FCSTD DOCUMENT  (FreeCAD 0.19R24276 (Git))
Label: Master_sketch_3
License: All rights reserved
LicenseURL: http://en.wikipedia.org/wiki/All_rights_reserved
objects: Sketcher::SketchObject×1, PartDesign::Body×1
note: 2 computed .brp shape members not serialized (recipe doc carries the construction recipe); baked Part::Feature solids carry a one-line shape summary decoded from their .brp

FEATURE [Sketcher::SketchObject] Sketch
  FullyConstrained = false
  MapMode = 5
  Support = -> [XY_Plane]
  sketch-geometry (160):
    g0: Circle CenterX=0 CenterY=0 CenterZ=0 NormalX=0 NormalY=0 NormalZ=1 AngleXU=0 Radius=30
    g1: Circle CenterX=0 CenterY=0 CenterZ=0 NormalX=0 NormalY=0 NormalZ=1 AngleXU=0 Radius=100
    g2: Circle CenterX=0 CenterY=-150 CenterZ=0 NormalX=0 NormalY=0 NormalZ=1 AngleXU=0 Radius=30
    g3: LineSegment StartX=-29.8748 StartY=-152.738 StartZ=0 EndX=-29.3845 EndY=-6.04557 EndZ=0
    g4: LineSegment StartX=29.8846 StartY=-152.629 StartZ=0 EndX=28.8668 EndY=-8.16756 EndZ=0
    g5: LineSegment StartX=0 StartY=0 StartZ=0 EndX=-44.858 EndY=-3.57179 EndZ=0
    g6: LineSegment StartX=0 StartY=0 StartZ=0 EndX=44.858 EndY=3.57179 EndZ=0
    g7: Circle CenterX=-44.858 CenterY=-3.57179 CenterZ=0 NormalX=0 NormalY=0 NormalZ=1 AngleXU=0 Radius=44
    g8: Circle CenterX=44.858 CenterY=3.57179 CenterZ=0 NormalX=0 NormalY=0 NormalZ=1 AngleXU=0 Radius=44
    g9: LineSegment StartX=0 StartY=0 StartZ=0 EndX=-29.9053 EndY=-2.38119 EndZ=0
    g10: Circle CenterX=-44.858 CenterY=-3.57179 CenterZ=0 NormalX=0 NormalY=0 NormalZ=1 AngleXU=0 Radius=12.5
    g11: Circle CenterX=0 CenterY=0 CenterZ=0 NormalX=0 NormalY=0 NormalZ=1 AngleXU=0 Radius=12.5
    g12: LineSegment StartX=-45.8502 StartY=8.88878 StartZ=0 EndX=-0.992163 EndY=12.4606 EndZ=0
    g13: LineSegment StartX=0.992163 StartY=-12.4606 StartZ=0 EndX=-43.8659 EndY=-16.0323 EndZ=0
    g14: Circle CenterX=44.858 CenterY=3.57179 CenterZ=0 NormalX=0 NormalY=0 NormalZ=1 AngleXU=0 Radius=21.9437
    g15: LineSegment StartX=279.194 StartY=89.253 StartZ=0 EndX=359.194 EndY=89.253 EndZ=0
    g16: LineSegment StartX=359.194 StartY=89.253 StartZ=0 EndX=359.194 EndY=78.253 EndZ=0
    g17: LineSegment StartX=359.194 StartY=78.253 StartZ=0 EndX=279.194 EndY=78.253 EndZ=0
    g18: LineSegment StartX=279.194 StartY=78.253 StartZ=0 EndX=279.194 EndY=89.253 EndZ=0
    g19: LineSegment StartX=294.194 StartY=89.253 StartZ=0 EndX=294.194 EndY=78.253 EndZ=0
    g20: LineSegment StartX=344.194 StartY=89.253 StartZ=0 EndX=344.194 EndY=78.253 EndZ=0
    g21: LineSegment StartX=279.194 StartY=78.253 StartZ=0 EndX=294.194 EndY=89.253 EndZ=0
    g22: LineSegment StartX=279.194 StartY=89.253 StartZ=0 EndX=294.194 EndY=78.253 EndZ=0
    g23: LineSegment StartX=344.194 StartY=78.253 StartZ=0 EndX=359.194 EndY=89.253 EndZ=0
    g24: LineSegment StartX=344.194 StartY=89.253 StartZ=0 EndX=359.194 EndY=78.253 EndZ=0
    g25: LineSegment StartX=279.194 StartY=107.893 StartZ=0 EndX=359.194 EndY=107.893 EndZ=0
    g26: LineSegment StartX=359.194 StartY=107.893 StartZ=0 EndX=359.194 EndY=118.893 EndZ=0
    g27: LineSegment StartX=359.194 StartY=118.893 StartZ=0 EndX=279.194 EndY=118.893 EndZ=0
    g28: LineSegment StartX=279.194 StartY=118.893 StartZ=0 EndX=279.194 EndY=107.893 EndZ=0
    g29: LineSegment StartX=294.194 StartY=107.893 StartZ=0 EndX=294.194 EndY=118.893 EndZ=0
    g30: LineSegment StartX=344.194 StartY=107.893 StartZ=0 EndX=344.194 EndY=118.893 EndZ=0
    g31: LineSegment StartX=279.194 StartY=118.893 StartZ=0 EndX=294.194 EndY=107.893 EndZ=0
    g32: LineSegment StartX=279.194 StartY=107.893 StartZ=0 EndX=294.194 EndY=118.893 EndZ=0
    g33: LineSegment StartX=344.194 StartY=118.893 StartZ=0 EndX=359.194 EndY=107.893 EndZ=0
    g34: LineSegment StartX=344.194 StartY=107.893 StartZ=0 EndX=359.194 EndY=118.893 EndZ=0
    g35: LineSegment StartX=279.194 StartY=155.729 StartZ=0 EndX=359.194 EndY=155.729 EndZ=0
    g36: LineSegment StartX=359.194 StartY=155.729 StartZ=0 EndX=359.194 EndY=144.729 EndZ=0
    g37: LineSegment StartX=359.194 StartY=144.729 StartZ=0 EndX=339.194 EndY=144.729 EndZ=0
    g38: LineSegment StartX=279.194 StartY=144.729 StartZ=0 EndX=279.194 EndY=155.729 EndZ=0
    g39: LineSegment StartX=294.194 StartY=155.729 StartZ=0 EndX=294.194 EndY=144.729 EndZ=0
    g40: LineSegment StartX=344.194 StartY=155.729 StartZ=0 EndX=344.194 EndY=144.729 EndZ=0
    g41: LineSegment StartX=279.194 StartY=144.729 StartZ=0 EndX=294.194 EndY=155.729 EndZ=0
    g42: LineSegment StartX=279.194 StartY=155.729 StartZ=0 EndX=294.194 EndY=144.729 EndZ=0
    g43: LineSegment StartX=344.194 StartY=144.729 StartZ=0 EndX=359.194 EndY=155.729 EndZ=0
    g44: LineSegment StartX=344.194 StartY=155.729 StartZ=0 EndX=359.194 EndY=144.729 EndZ=0
    g45: LineSegment StartX=226.201 StartY=102.55 StartZ=0 EndX=344.194 EndY=102.55 EndZ=0
    g46: LineSegment StartX=344.194 StartY=102.55 StartZ=0 EndX=344.194 EndY=93.5542 EndZ=0
    g47: LineSegment StartX=344.194 StartY=93.5542 StartZ=0 EndX=226.201 EndY=93.5542 EndZ=0
    g48: LineSegment StartX=226.201 StartY=93.5542 StartZ=0 EndX=226.201 EndY=102.55 EndZ=0
    g49: LineSegment StartX=295.194 StartY=126.307 StartZ=0 EndX=343.194 EndY=126.307 EndZ=0
    g50: LineSegment StartX=343.194 StartY=126.307 StartZ=0 EndX=343.194 EndY=74.3479 EndZ=0
    g51: LineSegment StartX=343.194 StartY=74.3479 StartZ=0 EndX=295.194 EndY=74.3479 EndZ=0
    g52: LineSegment StartX=295.194 StartY=74.3479 StartZ=0 EndX=295.194 EndY=93.5542 EndZ=0
    g53: LineSegment StartX=307.694 StartY=126.307 StartZ=0 EndX=332.694 EndY=126.307 EndZ=0
    g54: LineSegment StartX=332.694 StartY=126.307 StartZ=0 EndX=332.694 EndY=198.85 EndZ=0
    g55: LineSegment StartX=332.694 StartY=198.85 StartZ=0 EndX=307.694 EndY=198.85 EndZ=0
    g56: LineSegment StartX=307.694 StartY=198.85 StartZ=0 EndX=307.694 EndY=126.307 EndZ=0
    g57: LineSegment StartX=339.194 StartY=155.729 StartZ=0 EndX=339.194 EndY=144.729 EndZ=0
    g58: LineSegment StartX=334.194 StartY=130.474 StartZ=0 EndX=334.194 EndY=155.729 EndZ=0
    g59: LineSegment StartX=334.194 StartY=130.474 StartZ=0 EndX=363.584 EndY=130.474 EndZ=0
    g60: LineSegment StartX=377.854 StartY=142.729 StartZ=0 EndX=344.194 EndY=142.729 EndZ=0
    g61: LineSegment StartX=377.854 StartY=142.729 StartZ=0 EndX=377.854 EndY=69.4535 EndZ=0
    g62: LineSegment StartX=363.584 StartY=77.253 StartZ=0 EndX=363.584 EndY=98.9738 EndZ=0
    g63: LineSegment StartX=345.544 StartY=77.253 StartZ=0 EndX=363.584 EndY=77.253 EndZ=0
    g64: LineSegment StartX=345.544 StartY=69.3335 StartZ=0 EndX=345.544 EndY=77.253 EndZ=0
    g65: LineSegment StartX=345.544 StartY=106.893 StartZ=0 EndX=363.584 EndY=106.893 EndZ=0
    g66: LineSegment StartX=363.584 StartY=98.9738 StartZ=0 EndX=345.544 EndY=98.9738 EndZ=0
    g67: LineSegment StartX=345.544 StartY=98.9738 StartZ=0 EndX=345.544 EndY=106.893 EndZ=0
    g68: LineSegment StartX=363.584 StartY=106.893 StartZ=0 EndX=363.584 EndY=130.474 EndZ=0
    g69: LineSegment StartX=334.194 StartY=144.729 StartZ=0 EndX=279.194 EndY=144.729 EndZ=0
    g70: LineSegment StartX=295.194 StartY=102.55 StartZ=0 EndX=295.194 EndY=126.307 EndZ=0
    g71: LineSegment StartX=227.201 StartY=105.367 StartZ=0 EndX=248.6 EndY=105.367 EndZ=0
    g72: LineSegment StartX=248.6 StartY=105.367 StartZ=0 EndX=248.6 EndY=88.6412 EndZ=0
    g73: LineSegment StartX=248.6 StartY=88.6412 StartZ=0 EndX=227.201 EndY=88.6412 EndZ=0
    g74: LineSegment StartX=227.201 StartY=88.6412 StartZ=0 EndX=227.201 EndY=105.367 EndZ=0
    g75: LineSegment StartX=234.349 StartY=88.6412 StartZ=0 EndX=239.693 EndY=88.6412 EndZ=0
    g76: LineSegment StartX=239.693 StartY=88.6412 StartZ=0 EndX=239.693 EndY=81.4448 EndZ=0
    g77: LineSegment StartX=239.693 StartY=81.4448 StartZ=0 EndX=234.349 EndY=81.4448 EndZ=0
    g78: LineSegment StartX=234.349 StartY=81.4448 StartZ=0 EndX=234.349 EndY=88.6412 EndZ=0
    g79: LineSegment StartX=221.879 StartY=82.7173 StartZ=0 EndX=254.198 EndY=82.7173 EndZ=0
    g80: LineSegment StartX=254.198 StartY=82.7173 StartZ=0 EndX=254.198 EndY=30.8021 EndZ=0
    g81: LineSegment StartX=254.198 StartY=30.8021 StartZ=0 EndX=221.879 EndY=30.8021 EndZ=0
    g82: LineSegment StartX=221.879 StartY=30.8021 StartZ=0 EndX=221.879 EndY=82.7173 EndZ=0
    g83: LineSegment StartX=279.194 StartY=193.668 StartZ=0 EndX=359.194 EndY=193.668 EndZ=0
    g84: LineSegment StartX=359.194 StartY=193.668 StartZ=0 EndX=359.194 EndY=182.668 EndZ=0
    g85: LineSegment StartX=359.194 StartY=182.668 StartZ=0 EndX=279.194 EndY=182.668 EndZ=0
    g86: LineSegment StartX=279.194 StartY=182.668 StartZ=0 EndX=279.194 EndY=193.668 EndZ=0
    g87: LineSegment StartX=294.194 StartY=193.668 StartZ=0 EndX=294.194 EndY=182.668 EndZ=0
    g88: LineSegment StartX=344.194 StartY=193.668 StartZ=0 EndX=344.194 EndY=182.668 EndZ=0
    g89: LineSegment StartX=279.194 StartY=182.668 StartZ=0 EndX=294.194 EndY=193.668 EndZ=0
    g90: LineSegment StartX=279.194 StartY=193.668 StartZ=0 EndX=294.194 EndY=182.668 EndZ=0
    g91: LineSegment StartX=344.194 StartY=182.668 StartZ=0 EndX=359.194 EndY=193.668 EndZ=0
    g92: LineSegment StartX=344.194 StartY=193.668 StartZ=0 EndX=359.194 EndY=182.668 EndZ=0
    g93: LineSegment StartX=295.194 StartY=93.5542 StartZ=0 EndX=295.194 EndY=102.55 EndZ=0
    g94: LineSegment StartX=294.194 StartY=144.729 StartZ=0 EndX=243.792 EndY=144.729 EndZ=0
    g95: LineSegment StartX=243.792 StartY=144.729 StartZ=0 EndX=243.792 EndY=157.131 EndZ=0
    g96: LineSegment StartX=243.792 StartY=157.131 StartZ=0 EndX=281.594 EndY=157.131 EndZ=0
    g97: LineSegment StartX=294.194 StartY=156.804 StartZ=0 EndX=294.194 EndY=144.729 EndZ=0
    g98: LineSegment StartX=344.194 StartY=144.729 StartZ=0 EndX=394.596 EndY=144.729 EndZ=0
    g99: LineSegment StartX=394.596 StartY=144.729 StartZ=0 EndX=394.596 EndY=157.131 EndZ=0
    g100: LineSegment StartX=394.596 StartY=157.131 StartZ=0 EndX=356.794 EndY=157.131 EndZ=0
    g101: LineSegment StartX=344.194 StartY=157.131 StartZ=0 EndX=344.194 EndY=144.729 EndZ=0
    g102: LineSegment StartX=252.412 StartY=146.599 StartZ=0 EndX=170.647 EndY=146.599 EndZ=0
    g103: LineSegment StartX=170.647 StartY=146.599 StartZ=0 EndX=170.647 EndY=155.302 EndZ=0
    g104: LineSegment StartX=170.647 StartY=155.302 StartZ=0 EndX=252.412 EndY=155.302 EndZ=0
    g105: LineSegment StartX=252.412 StartY=155.302 StartZ=0 EndX=252.412 EndY=146.599 EndZ=0
    g106: LineSegment StartX=174.377 StartY=158.1 StartZ=0 EndX=197.379 EndY=158.1 EndZ=0
    g107: LineSegment StartX=197.379 StartY=158.1 StartZ=0 EndX=197.379 EndY=144.14 EndZ=0
    g108: LineSegment StartX=197.379 StartY=144.14 StartZ=0 EndX=174.377 EndY=144.14 EndZ=0
    g109: LineSegment StartX=174.377 StartY=144.14 StartZ=0 EndX=174.377 EndY=158.1 EndZ=0
    g110: LineSegment StartX=181.526 StartY=144.14 StartZ=0 EndX=188.675 EndY=144.14 EndZ=0
    g111: LineSegment StartX=188.675 StartY=144.14 StartZ=0 EndX=188.675 EndY=138.828 EndZ=0
    g112: LineSegment StartX=188.675 StartY=138.828 StartZ=0 EndX=181.526 EndY=138.828 EndZ=0
    g113: LineSegment StartX=181.526 StartY=138.828 StartZ=0 EndX=181.526 EndY=144.14 EndZ=0
    g114: LineSegment StartX=169.404 StartY=139.139 StartZ=0 EndX=203.285 EndY=139.139 EndZ=0
    g115: LineSegment StartX=203.285 StartY=139.139 StartZ=0 EndX=203.285 EndY=67.3373 EndZ=0
    g116: LineSegment StartX=203.285 StartY=67.3373 StartZ=0 EndX=169.404 EndY=67.3373 EndZ=0
    g117: LineSegment StartX=169.404 StartY=67.3373 StartZ=0 EndX=169.404 EndY=139.139 EndZ=0
    g118: LineSegment StartX=344.194 StartY=144.729 StartZ=0 EndX=344.194 EndY=142.729 EndZ=0
    g119: LineSegment StartX=345.544 StartY=69.4535 StartZ=0 EndX=345.544 EndY=20.25 EndZ=0
    g120: LineSegment StartX=345.544 StartY=20.25 StartZ=0 EndX=377.854 EndY=20.25 EndZ=0
    g121: LineSegment StartX=377.854 StartY=20.25 StartZ=0 EndX=377.854 EndY=69.4535 EndZ=0
    g122: LineSegment StartX=292.844 StartY=77.253 StartZ=0 EndX=260.534 EndY=77.253 EndZ=0
    g123: LineSegment StartX=260.534 StartY=77.253 StartZ=0 EndX=260.534 EndY=20.25 EndZ=0
    g124: LineSegment StartX=260.534 StartY=20.25 StartZ=0 EndX=292.844 EndY=20.25 EndZ=0
    g125: LineSegment StartX=292.844 StartY=20.25 StartZ=0 EndX=292.844 EndY=77.253 EndZ=0
    g126: LineSegment StartX=377.854 StartY=20.25 StartZ=0 EndX=215.589 EndY=20.25 EndZ=0
    g127: LineSegment StartX=215.589 StartY=20.25 StartZ=0 EndX=215.589 EndY=13.0105 EndZ=0
    g128: LineSegment StartX=215.589 StartY=13.0105 StartZ=0 EndX=377.854 EndY=13.0105 EndZ=0
    g129: LineSegment StartX=377.854 StartY=13.0105 StartZ=0 EndX=377.854 EndY=20.25 EndZ=0
    g130: LineSegment StartX=430.194 StartY=201.048 StartZ=0 EndX=510.194 EndY=201.048 EndZ=0
    g131: LineSegment StartX=510.194 StartY=201.048 StartZ=0 EndX=510.194 EndY=212.048 EndZ=0
    g132: LineSegment StartX=510.194 StartY=212.048 StartZ=0 EndX=430.194 EndY=212.048 EndZ=0
    g133: LineSegment StartX=430.194 StartY=212.048 StartZ=0 EndX=430.194 EndY=201.048 EndZ=0
    g134: LineSegment StartX=445.194 StartY=201.048 StartZ=0 EndX=445.194 EndY=212.048 EndZ=0
    g135: LineSegment StartX=495.194 StartY=201.048 StartZ=0 EndX=495.194 EndY=212.048 EndZ=0
    g136: LineSegment StartX=430.194 StartY=212.048 StartZ=0 EndX=445.194 EndY=201.048 EndZ=0
    g137: LineSegment StartX=430.194 StartY=201.048 StartZ=0 EndX=445.194 EndY=212.048 EndZ=0
    g138: LineSegment StartX=495.194 StartY=212.048 StartZ=0 EndX=510.194 EndY=201.048 EndZ=0
    g139: LineSegment StartX=495.194 StartY=201.048 StartZ=0 EndX=510.194 EndY=212.048 EndZ=0
    g140: LineSegment StartX=320.194 StartY=6.98585 StartZ=0 EndX=320.194 EndY=198.85 EndZ=0
    g141: LineSegment StartX=470.194 StartY=234.881 StartZ=0 EndX=470.194 EndY=201.048 EndZ=0
    g142: LineSegment StartX=281.594 StartY=157.131 StartZ=0 EndX=281.594 EndY=174.057 EndZ=0
    g143: LineSegment StartX=281.594 StartY=174.057 StartZ=0 EndX=294.194 EndY=174.057 EndZ=0
    g144: LineSegment StartX=294.194 StartY=174.057 StartZ=0 EndX=294.194 EndY=156.804 EndZ=0
    g145: LineSegment StartX=356.794 StartY=157.131 StartZ=0 EndX=356.794 EndY=174.057 EndZ=0
    g146: LineSegment StartX=356.794 StartY=174.057 StartZ=0 EndX=344.194 EndY=174.057 EndZ=0
    g147: LineSegment StartX=344.194 StartY=174.057 StartZ=0 EndX=344.194 EndY=157.131 EndZ=0
    g148: LineSegment StartX=351.103 StartY=170.103 StartZ=0 EndX=498.037 EndY=170.103 EndZ=0
    g149: LineSegment StartX=498.037 StartY=170.103 StartZ=0 EndX=498.037 EndY=163.51 EndZ=0
    g150: LineSegment StartX=498.037 StartY=163.51 StartZ=0 EndX=351.103 EndY=163.51 EndZ=0
    g151: LineSegment StartX=351.103 StartY=163.51 StartZ=0 EndX=351.103 EndY=170.103 EndZ=0
    g152: LineSegment StartX=451.917 StartY=158.051 StartZ=0 EndX=492.067 EndY=158.051 EndZ=0
    g153: LineSegment StartX=492.067 StartY=259.442 StartZ=0 EndX=451.917 EndY=259.442 EndZ=0
    g154: LineSegment StartX=451.917 StartY=259.442 StartZ=0 EndX=451.917 EndY=158.051 EndZ=0
    g155: LineSegment StartX=307.694 StartY=198.85 StartZ=0 EndX=513.266 EndY=198.85 EndZ=0
    g156: LineSegment StartX=513.266 StartY=198.85 StartZ=0 EndX=513.266 EndY=214.548 EndZ=0
    g157: LineSegment StartX=513.266 StartY=214.548 StartZ=0 EndX=307.694 EndY=214.548 EndZ=0
    g158: LineSegment StartX=307.694 StartY=214.548 StartZ=0 EndX=307.694 EndY=198.85 EndZ=0
    g159: LineSegment StartX=492.067 StartY=259.442 StartZ=0 EndX=492.067 EndY=158.051 EndZ=0
  constraints (393):
    c: Coincident(g0,g-1)
    c: Coincident(g1,g-1)
    c: PointOnObject(g2,g-2)
    c: PointOnObject(g3,g2)
    c: PointOnObject(g3,g0)
    c: PointOnObject(g4,g2)
    c: PointOnObject(g4,g0)
    c: Coincident(g5,g-1)
    c: Coincident(g6,g-1)
    c: Parallel(g5,g6)
    c: Equal(g6,g5)
    c: Coincident(g7,g5)
    c: Coincident(g8,g6)
    c: Equal(g7,g8)
    c: Coincident(g9,g-1)
    c: PointOnObject(g9,g0)
    c: Parallel(g9,g5)
    c: Distance(g6) = 45
    c: Diameter(g8) = 88
    c: Diameter(g1) = 200
    c: Diameter(g0) = 60
    c: Equal(g2,g0)
    c: DistanceY(g2,g-1) = 150
    c: Coincident(g10,g5)
    c: Coincident(g11,g-1)
    c: PointOnObject(g12,g10)
    c: PointOnObject(g12,g11)
    c: Tangent(g12,g10)
    c: Equal(g10,g11)
    c: PointOnObject(g13,g11)
    c: PointOnObject(g13,g10)
    c: Tangent(g13,g10)
    c: Parallel(g13,g12)
    c: Diameter(g10) = 25
    c: Coincident(g14,g6)
    c: Coincident(g15,g16)
    c: Coincident(g16,g17)
    c: Coincident(g17,g18)
    c: Coincident(g18,g15)
    c: Horizontal(g15)
    c: Horizontal(g17)
    c: Vertical(g16)
    c: Vertical(g18)
    c: PointOnObject(g19,g15)
    c: PointOnObject(g19,g17)
    c: Vertical(g19)
    c: PointOnObject(g20,g15)
    c: Vertical(g20)
    c: DistanceX(g17,g17) = 80
    c: DistanceX(g19,g20) = 50
    c: DistanceY(g18,g18) = 11
    c: Coincident(g21,g17)
    c: Coincident(g21,g19)
    c: Coincident(g22,g15)
    c: Coincident(g22,g19)
    c: Coincident(g23,g20)
    c: Coincident(g23,g15)
    c: Coincident(g24,g20)
    c: Coincident(g24,g16)
    c: DistanceX(g17,g19) = 15
    c: Coincident(g25,g26)
    c: Coincident(g26,g27)
    c: Coincident(g27,g28)
    c: Coincident(g28,g25)
    c: Horizontal(g25)
    c: Horizontal(g27)
    c: Vertical(g26)
    c: Vertical(g28)
    c: PointOnObject(g29,g25)
    c: PointOnObject(g29,g27)
    c: Vertical(g29)
    c: PointOnObject(g30,g25)
    c: Vertical(g30)
    c: Coincident(g31,g27)
    c: Coincident(g31,g29)
    c: Coincident(g32,g25)
    c: Coincident(g32,g29)
    c: Coincident(g33,g30)
    c: Coincident(g33,g25)
    c: Coincident(g34,g30)
    c: Coincident(g34,g26)
    c: Coincident(g35,g36)
    c: Coincident(g36,g37)
    c: Coincident(g69,g38)
    c: Coincident(g38,g35)
    c: Horizontal(g35)
    c: Horizontal(g37)
    c: Vertical(g36)
    c: Vertical(g38)
    c: PointOnObject(g39,g35)
    c: PointOnObject(g39,g37)
    c: Vertical(g39)
    c: PointOnObject(g40,g35)
    c: Vertical(g40)
    c: Coincident(g41,g69)
    c: Coincident(g41,g39)
    c: Coincident(g42,g35)
    c: Coincident(g42,g39)
    c: Coincident(g43,g40)
    c: Coincident(g43,g35)
    c: Coincident(g44,g40)
    c: Coincident(g44,g36)
    c: Equal(g25,g17)
    c: Equal(g16,g26)
    c: Equal(g30,g26)
    c: Equal(g31,g22)
    c: Equal(g34,g23)
    c: Horizontal(g20,g16)
    c: Horizontal(g40,g36)
    c: Equal(g36,g26)
    c: Equal(g33,g44)
    c: Equal(g42,g31)
    c: Vertical(g19,g29)
    c: Vertical(g29,g39)
    c: Coincident(g45,g46)
    c: Coincident(g46,g47)
    c: Coincident(g47,g48)
    c: Coincident(g48,g45)
    c: Horizontal(g45)
    c: Horizontal(g47)
    c: Vertical(g46)
    c: Vertical(g48)
    c: Coincident(g49,g50)
    c: Coincident(g50,g51)
    c: Coincident(g51,g52)
    c: Coincident(g70,g49)
    c: Horizontal(g49)
    c: Horizontal(g51)
    c: Vertical(g50)
    c: Vertical(g52)
    c: DistanceX(g51,g51) = 48
    c: DistanceX(g19,g51) = 1
    c: Coincident(g53,g54)
    c: Coincident(g54,g55)
    c: Coincident(g55,g56)
    c: Coincident(g56,g53)
    c: Horizontal(g53)
    c: Horizontal(g55)
    c: Vertical(g54)
    c: Vertical(g56)
    c: PointOnObject(g53,g49)
    c: DistanceX(g55,g54) = 25
    c: DistanceX(g49,g53) = 12.5
    c: Vertical(g57)
    c: Vertical(g58)
    c: Horizontal(g59)
    c: Horizontal(g60)
    c: Vertical(g61)
    c: Vertical(g62)
    c: Coincident(g64,g63)
    c: Horizontal(g63)
    c: Vertical(g64)
    c: Coincident(g66,g67)
    c: Coincident(g67,g65)
    c: Horizontal(g65)
    c: Horizontal(g66)
    c: Vertical(g67)
    c: Tangent(g62,g68)
    c: Equal(g64,g67)
    c: Vertical(g63,g66)
    c: PointOnObject(g58,g35)
    c: PointOnObject(g57,g35)
    c: PointOnObject(g69,g58)
    c: Tangent(g37,g69)
    c: Coincident(g60,g61)
    c: Coincident(g63,g62)
    c: Coincident(g62,g66)
    c: Coincident(g65,g68)
    c: PointOnObject(g52,g47)
    c: PointOnObject(g70,g45)
    c: Tangent(g52,g70)
    c: Coincident(g71,g72)
    c: Coincident(g72,g73)
    c: Coincident(g73,g74)
    c: Coincident(g74,g71)
    c: Horizontal(g71)
    c: Horizontal(g73)
    c: Vertical(g72)
    c: Vertical(g74)
    c: Coincident(g75,g76)
    c: Coincident(g76,g77)
    c: Coincident(g77,g78)
    c: Coincident(g78,g75)
    c: Horizontal(g75)
    c: Horizontal(g77)
    c: Vertical(g76)
    c: Vertical(g78)
    c: PointOnObject(g75,g73)
    c: Coincident(g79,g80)
    c: Coincident(g80,g81)
    c: Coincident(g81,g82)
    c: Coincident(g82,g79)
    c: Horizontal(g79)
    c: Horizontal(g81)
    c: Vertical(g80)
    c: Vertical(g82)
    c: Coincident(g83,g84)
    c: Coincident(g84,g85)
    c: Coincident(g85,g86)
    c: Coincident(g86,g83)
    c: Horizontal(g83)
    c: Horizontal(g85)
    c: Vertical(g84)
    c: Vertical(g86)
    c: PointOnObject(g87,g83)
    c: PointOnObject(g87,g85)
    c: Vertical(g87)
    c: PointOnObject(g88,g83)
    c: Vertical(g88)
    c: Coincident(g89,g85)
    c: Coincident(g89,g87)
    c: Coincident(g90,g83)
    c: Coincident(g90,g87)
    c: Coincident(g91,g88)
    c: Coincident(g91,g83)
    c: Coincident(g92,g88)
    c: Coincident(g92,g84)
    c: Equal(g88,g84)
    c: Equal(g85,g35)
    c: Equal(g84,g36)
    c: Equal(g92,g44)
    c: Equal(g90,g42)
    c: Equal(g17,g83)
    c: Vertical(g85,g15)
    c: DistanceX(g20,g63) = 1.35
    c: DistanceX(g64,g61) = 32.31
    c: DistanceX(g63,g63) = 18.04
    c: DistanceY(g62,g16) = 1
    c: DistanceY(g65,g25) = 1
    c: DistanceY(g60,g36) = 2
    c: DistanceX(g57,g40) = 5
    c: Coincident(g59,g68)
    c: DistanceX(g50,g46) = 1
    c: DistanceX(g47,g73) = 1
    c: Coincident(g93,g52)
    c: Coincident(g94,g95)
    c: Coincident(g95,g96)
    c: Coincident(g97,g94)
    c: Horizontal(g94)
    c: Horizontal(g96)
    c: Vertical(g95)
    c: Vertical(g97)
    c: Coincident(g94,g39)
    c: Coincident(g98,g99)
    c: Coincident(g99,g100)
    c: Coincident(g101,g98)
    c: Horizontal(g98)
    c: Horizontal(g100)
    c: Vertical(g99)
    c: Vertical(g101)
    c: Coincident(g98,g40)
    c: Coincident(g58,g59)
    c: Coincident(g102,g103)
    c: Coincident(g103,g104)
    c: Coincident(g104,g105)
    c: Coincident(g105,g102)
    c: Horizontal(g102)
    c: Horizontal(g104)
    c: Vertical(g103)
    c: Vertical(g105)
    c: Coincident(g106,g107)
    c: Coincident(g107,g108)
    c: Coincident(g108,g109)
    c: Coincident(g109,g106)
    c: Horizontal(g106)
    c: Horizontal(g108)
    c: Vertical(g107)
    c: Vertical(g109)
    c: Coincident(g110,g111)
    c: Coincident(g111,g112)
    c: Coincident(g112,g113)
    c: Coincident(g113,g110)
    c: Horizontal(g110)
    c: Horizontal(g112)
    c: Vertical(g111)
    c: Vertical(g113)
    c: PointOnObject(g110,g108)
    c: Coincident(g114,g115)
    c: Coincident(g115,g116)
    c: Coincident(g116,g117)
    c: Coincident(g117,g114)
    c: Horizontal(g114)
    c: Horizontal(g116)
    c: Vertical(g115)
    c: Vertical(g117)
    c: Coincident(g118,g40)
    c: Vertical(g118)
    c: Coincident(g60,g118)
    c: Coincident(g57,g37)
    c: Coincident(g119,g120)
    c: Coincident(g120,g121)
    c: Horizontal(g120)
    c: Vertical(g119)
    c: Vertical(g121)
    c: Coincident(g122,g123)
    c: Coincident(g123,g124)
    c: Coincident(g124,g125)
    c: Coincident(g125,g122)
    c: Horizontal(g122)
    c: Horizontal(g124)
    c: Vertical(g123)
    c: Vertical(g125)
    c: Horizontal(g124,g119)
    c: Equal(g124,g120)
    c: Vertical(g64,g119)
    c: Coincident(g126,g127)
    c: Coincident(g127,g128)
    c: Coincident(g128,g129)
    c: Coincident(g129,g126)
    c: Horizontal(g126)
    c: Horizontal(g128)
    c: Vertical(g127)
    c: Vertical(g129)
    c: Coincident(g126,g120)
    c: Coincident(g93,g70)
    c: Coincident(g130,g131)
    c: Coincident(g131,g132)
    c: Coincident(g132,g133)
    c: Coincident(g133,g130)
    c: Horizontal(g130)
    c: Vertical(g131)
    c: Vertical(g133)
    c: PointOnObject(g134,g130)
    c: PointOnObject(g134,g132)
    c: Vertical(g134)
    c: PointOnObject(g135,g130)
    c: Vertical(g135)
    c: Coincident(g136,g132)
    c: Coincident(g136,g134)
    c: Coincident(g137,g130)
    c: Coincident(g137,g134)
    c: Coincident(g138,g135)
    c: Coincident(g138,g130)
    c: Coincident(g139,g135)
    c: Coincident(g139,g131)
    c: Equal(g135,g131)
    c: Equal(g130,g85)
    c: Equal(g131,g84)
    c: Equal(g84,g133)
    c: Parallel(g139,g91)
    c: Parallel(g136,g90)
    c: Vertical(g140)
    c: Symmetric(g55,g54,g140)
    c: Vertical(g141)
    c: Symmetric(g130,g130,g141)
    c: DistanceX(g140,g141) = 150
    c: Coincident(g142,g143)
    c: Coincident(g143,g144)
    c: Horizontal(g143)
    c: Vertical(g142)
    c: Vertical(g144)
    c: Coincident(g145,g146)
    c: Coincident(g146,g147)
    c: Horizontal(g146)
    c: Vertical(g145)
    c: Vertical(g147)
    c: Horizontal(g143,g146)
    c: Equal(g143,g146)
    c: Coincident(g97,g144)
    c: Coincident(g142,g96)
    c: Coincident(g145,g100)
    c: Coincident(g101,g147)
    c: Coincident(g61,g121)
    c: Equal(g98,g94)
    c: DistanceX(g58,g57) = 5
    c: DistanceX(g122,g19) = 1.35
    c: DistanceX(g95,g104) = 8.62
    c: Coincident(g148,g149)
    c: Coincident(g149,g150)
    c: Coincident(g150,g151)
    c: Coincident(g151,g148)
    c: Horizontal(g148)
    c: Horizontal(g150)
    c: Vertical(g149)
    c: Vertical(g151)
    c: Coincident(g153,g154)
    c: Coincident(g154,g152)
    c: Horizontal(g152)
    c: Horizontal(g153)
    c: Vertical(g154)
    c: Coincident(g155,g156)
    c: Coincident(g156,g157)
    c: Coincident(g157,g158)
    c: Coincident(g158,g155)
    c: Horizontal(g155)
    c: Horizontal(g157)
    c: Vertical(g156)
    c: Vertical(g158)
    c: Coincident(g155,g55)
    c: Vertical(g159)
    c: Coincident(g159,g152)
    c: Coincident(g153,g159)
    c: Horizontal(g122,g63)
FEATURE [PartDesign::Body] Body
  Group = -> [Sketch]
  Origin = -> Origin
